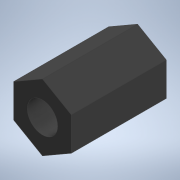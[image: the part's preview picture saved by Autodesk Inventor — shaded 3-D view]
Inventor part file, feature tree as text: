
AUTODESK INVENTOR PART (.ipt)
format: ipt  version: 2020 (Build 240168000, 168)  size: 97,280 bytes
history: native  units: mm
features: extrude x1, sketch x1
ambient origin geometry x8: Origin, YZ Plane, XZ Plane, XY Plane, X Axis, Y Axis, Z Axis, Center Point
bodies: Solid1 (feature_tree)
feature tree (2):
  extrude  "Extrusion1"  Depth=3.5mm
  sketch  "Sketch1"  dims[d0=3.2mm d1=3.5mm d2=10.0mm d3=0.0mm]
